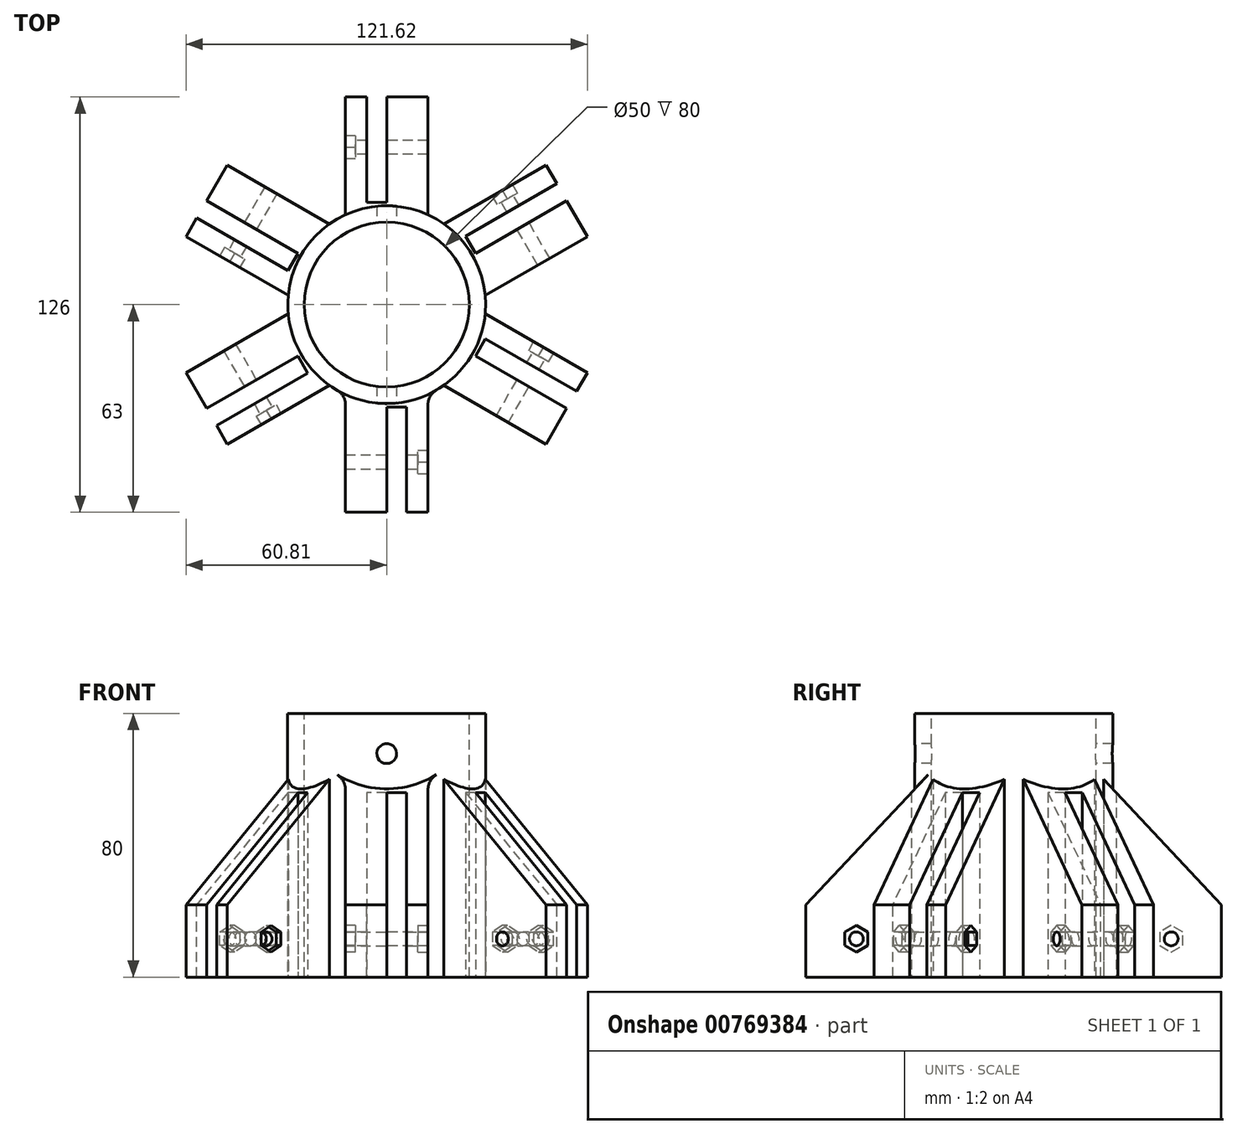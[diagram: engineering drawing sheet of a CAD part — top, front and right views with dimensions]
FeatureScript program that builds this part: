
annotation { "Feature Type Name" : "Feature", "Feature Type Description" : "" }
export const myFeature = defineFeature(function(context is Context, id is Id, definition is map)
    precondition{}
    {
        {
            var Q0;
            Q0=qCreatedBy(makeId("Top.planeOp"),FACE);
            var sketch = newSketch(context, id + "F0", { "sketchPlane" : qUnion([Q0])});
            skCircle(sketch, "E0", {"center": v(0, 0) * mm, "radius": 30 * mm});
            skSolve(sketch);
        }
        {
            var Q0;
            Q0=qSketchRegion(id+"F0",true);
            var Q1;
            Q1=qSketchRegion(id+"F2",true);
            extrude(context, id + "F1", {"entities" : qUnion([Q0, Q1]), "depth" : 60 * mm, "offsetDistance" : 25 * mm});
        }
        {
            var Q0;
            Q0=qCreatedBy(makeId("Front.planeOp"),FACE);
            var sketch = newSketch(context, id + "F2", { "sketchPlane" : qUnion([Q0])});
            skLineSegment(sketch, "E1.bottom", {"start": v(-12.5, 0) * mm, "end": v(12.5, 0) * mm});
            skLineSegment(sketch, "E1.top", {"start": v(-12.5, 60) * mm, "end": v(12.5, 60) * mm});
            skLineSegment(sketch, "E1.left", {"start": v(-12.5, 0) * mm, "end": v(-12.5, 60) * mm});
            skLineSegment(sketch, "E1.right", {"start": v(12.5, 0) * mm, "end": v(12.5, 60) * mm});
            skSolve(sketch);
        }
        {
            var Q0;
            Q0=qSketchRegion(id+"F2",true);
            var Q1;
            Q1=qSketchRegion(id+"F4",true);
            extrude(context, id + "F3", {"entities" : qUnion([Q0, Q1]), "operationType" : NewBodyOperationType.ADD, "depth" : 63 * mm, "offsetDistance" : 25 * mm});
        }
        {
            var Q0;
            Q0=makeQuery(id+"F3.opExtrude","SWEPT_FACE",FACE,{"disambiguationData":[OSD([sQuery(id+"F2.wireOp",EDGE,"E1.right")])]});
            var sketch = newSketch(context, id + "F4", { "sketchPlane" : qUnion([Q0])});
            skLineSegment(sketch, "E2", {"start": v(-27.27, 60) * mm, "end": v(-63, 21.96) * mm});
            skLineSegment(sketch, "E3", {"start": v(-63, 21.96) * mm, "end": v(-63, 60) * mm});
            skLineSegment(sketch, "E4", {"start": v(-63, 60) * mm, "end": v(-27.27, 60) * mm});
            skSolve(sketch);
        }
        {
            var Q0;
            Q0=qSketchRegion(id+"F4",true);
            var Q1;
            Q1=qSketchRegion(id+"FgFtPWKNHrMfXQx_1",true);
            extrude(context, id + "F5", {"entities" : qUnion([Q0, Q1]), "operationType" : NewBodyOperationType.REMOVE, "oppositeDirection" : true, "depth" : 25 * mm, "offsetDistance" : 25 * mm});
        }
        {
            var Q0;
            Q0=qCreatedBy(makeId("Top.planeOp"),FACE);
            var sketch = newSketch(context, id + "F6", { "sketchPlane" : qUnion([Q0])});
            skLineSegment(sketch, "E5.left", {"start": v(0, -31.08) * mm, "end": v(0, -63.76) * mm});
            skLineSegment(sketch, "E5.right", {"start": v(6, -31.08) * mm, "end": v(6, -63.76) * mm});
            skLineSegment(sketch, "E6.bottom", {"start": v(0, -31.08) * mm, "end": v(6, -31.08) * mm});
            skLineSegment(sketch, "E6.top", {"start": v(0, -63.76) * mm, "end": v(6, -63.76) * mm});
            skPoint(sketch, "E5.bottom.start.orphan", {"position": v(0, -30.09) * mm});
            skSolve(sketch);
        }
        {
            var Q0;
            Q0=qSketchRegion(id+"F6",true);
            var Q1;
            Q1=makeQuery(id+"F5.boolean.opBoolean","COPY",FACE,{"derivedFrom":makeQuery(id+"F5.opExtrude","SWEPT_FACE",FACE,{"disambiguationData":[OSD([sQuery(id+"F4.wireOp",EDGE,"E2")])]})});
            extrude(context, id + "F7", {"entities" : qUnion([Q0, Q1]), "operationType" : NewBodyOperationType.REMOVE, "depth" : 114.6 * mm, "offsetDistance" : 25 * mm});
        }
        {
            var Q0;
            Q0=makeQuery(id+"F3.opExtrude","SWEPT_FACE",FACE,{"disambiguationData":[OSD([sQuery(id+"F2.wireOp",EDGE,"E1.right")])]});
            var sketch = newSketch(context, id + "F8", { "sketchPlane" : qUnion([Q0])});
            skCircle(sketch, "E7", {"center": v(-47.71, 11.61) * mm, "radius": 2.1 * mm});
            skPoint(sketch, "E8.0.midPoint", {"position": v(-44.21, 11.61) * mm});
            skCircle(sketch, "E9.cCircle", {"center": v(-47.71, 11.61) * mm, "radius": 3.5 * mm, "construction": true});
            skLineSegment(sketch, "E9.0", {"start": v(-44.21, 13.63) * mm, "end": v(-44.21, 9.6) * mm});
            skLineSegment(sketch, "E9.1", {"start": v(-44.21, 9.6) * mm, "end": v(-47.71, 7.57) * mm});
            skLineSegment(sketch, "E9.2", {"start": v(-47.71, 7.57) * mm, "end": v(-51.21, 9.6) * mm});
            skLineSegment(sketch, "E9.3", {"start": v(-51.21, 9.6) * mm, "end": v(-51.21, 13.63) * mm});
            skLineSegment(sketch, "E9.4", {"start": v(-51.21, 13.63) * mm, "end": v(-47.71, 15.66) * mm});
            skLineSegment(sketch, "E9.5", {"start": v(-47.71, 15.66) * mm, "end": v(-44.21, 13.63) * mm});
            skSolve(sketch);
        }
        {
            var Q0;
            Q0 = qSketchRegion(id + "F8", true);
            extrude(context, id + "F9", {"entities" : qUnion([Q0]), "operationType" : NewBodyOperationType.REMOVE, "oppositeDirection" : true, "depth" : 3 * mm, "offsetDistance" : 25 * mm});
        }
        {
            var Q0;
            Q0=sQuery(id+"F8.wireOp",VERTEX,"XOagpPQl-PvC6-i4lp-4W3e-Tbm5HYOVrYsB.center");
            var Q1;
            Q1=sQuery(id+"F8.wireOp",VERTEX,"E7.center");
            var Q2;
            Q2=makeQuery(id+"F1.opExtrude","SWEPT_BODY",BODY,{"disambiguationData":[OSD([sQuery(id+"F0.wireOp",EDGE,"E0")])]});
            hole(context, id + "F10", {"style" : HoleStyle.SIMPLE, "endStyle" : HoleEndStyle.THROUGH, "holeDiameter" : 4.2 * mm, "majorDiameter" : 5 * mm, "isTappedThrough" : true, "tappedDepth" : 12 * mm, "tapClearance" : 3, "locations" : qUnion([Q0, Q1]), "scope" : qUnion([Q2])});
        }
        {
            var Q0;
            Q0=makeQuery(id+"F1.opExtrude","SWEPT_BODY",BODY,{"disambiguationData":[OSD([sQuery(id+"F0.wireOp",EDGE,"E0")])]});
            var Q1;
            Q1=makeQuery(id+"F1.opExtrude","SWEPT_FACE",FACE,{"disambiguationData":[OSD([sQuery(id+"F0.wireOp",EDGE,"E0")])]});
            circularPattern(context, id + "F11", {"operationType" : NewBodyOperationType.ADD, "entities" : qUnion([Q0]), "axis" : qUnion([Q1]), "angle" : 360 * degree, "instanceCount" : 6, "equalSpace" : true});
        }
        {
            var Q0;
            {var subQ0=makeQuery(id+"F3.boolean.opBoolean","MERGE",FACE,{"derivedFrom":[makeQuery(id+"F1.opExtrude","CAP_FACE",FACE,{"disambiguationData":[OSD([sQuery(id+"F0.wireOp",EDGE,"E0")])],"isStart":false}),makeQuery(id+"F3.opExtrude","SWEPT_FACE",FACE,{"disambiguationData":[OSD([sQuery(id+"F2.wireOp",EDGE,"E1.top")])]})]});Q0=makeQuery(id+"F11.boolean.opBoolean","MERGE",FACE,{"derivedFrom":[subQ0,makeQuery(id+"F11.opPattern","COPY",FACE,{"derivedFrom":subQ0,"instanceName":"1"}),makeQuery(id+"F11.opPattern","COPY",FACE,{"derivedFrom":subQ0,"instanceName":"2"}),makeQuery(id+"F11.opPattern","COPY",FACE,{"derivedFrom":subQ0,"instanceName":"3"}),makeQuery(id+"F11.opPattern","COPY",FACE,{"derivedFrom":subQ0,"instanceName":"4"}),makeQuery(id+"F11.opPattern","COPY",FACE,{"derivedFrom":subQ0,"instanceName":"5"})]});}
            var sketch = newSketch(context, id + "F12", { "sketchPlane" : qUnion([Q0])});
            skCircle(sketch, "E10", {"center": v(0, 0) * mm, "radius": 25 * mm});
            skSolve(sketch);
        }
        {
            var Q0;
            Q0=makeQuery(id+"F12.imprint","IMPRINT",FACE,{"disambiguationData":[TD([[makeQuery(id+"F12.imprint","IMPRINT",EDGE,{"derivedFrom":sQuery(id+"F12.wireOp",EDGE,"E10")}),1.0]])]});
            extrude(context, id + "F13", {"entities" : qUnion([Q0]), "operationType" : NewBodyOperationType.REMOVE, "endBound" : BoundingType.THROUGH_ALL, "oppositeDirection" : true, "depth" : 25 * mm, "offsetDistance" : 25 * mm});
        }
        {
            var Q0;
            {var subQ0=makeQuery(id+"F3.boolean.opBoolean","MERGE",FACE,{"derivedFrom":[makeQuery(id+"F1.opExtrude","CAP_FACE",FACE,{"disambiguationData":[OSD([sQuery(id+"F0.wireOp",EDGE,"E0")])],"isStart":false}),makeQuery(id+"F3.opExtrude","SWEPT_FACE",FACE,{"disambiguationData":[OSD([sQuery(id+"F2.wireOp",EDGE,"E1.top")])]})]});Q0=makeQuery(id+"F11.boolean.opBoolean","MERGE",FACE,{"derivedFrom":[subQ0,makeQuery(id+"F11.opPattern","COPY",FACE,{"derivedFrom":subQ0,"instanceName":"1"}),makeQuery(id+"F11.opPattern","COPY",FACE,{"derivedFrom":subQ0,"instanceName":"2"}),makeQuery(id+"F11.opPattern","COPY",FACE,{"derivedFrom":subQ0,"instanceName":"3"}),makeQuery(id+"F11.opPattern","COPY",FACE,{"derivedFrom":subQ0,"instanceName":"4"}),makeQuery(id+"F11.opPattern","COPY",FACE,{"derivedFrom":subQ0,"instanceName":"5"})]});}
            extrude(context, id + "F14", {"entities" : qUnion([Q0]), "operationType" : NewBodyOperationType.ADD, "depth" : 20 * mm, "offsetDistance" : 25 * mm});
        }
        {
            var Q0;
            Q0=makeQuery(id+"F3.boolean.opBoolean","INTERSECT",EDGE,{"derivedFrom":[makeQuery(id+"F1.opExtrude","SWEPT_FACE",FACE,{"disambiguationData":[OSD([sQuery(id+"F0.wireOp",EDGE,"E0")])]}),makeQuery(id+"F3.opExtrude","SWEPT_FACE",FACE,{"disambiguationData":[OSD([sQuery(id+"F2.wireOp",EDGE,"E1.right")])]})]});
            var Q1;
            {var subQ0=makeQuery(id+"F1.opExtrude","SWEPT_FACE",FACE,{"disambiguationData":[OSD([sQuery(id+"F0.wireOp",EDGE,"E0")])]});var subQ1=subQ0;Q1=makeQuery(id+"F11.boolean.opBoolean","INTERSECT",EDGE,{"disambiguationData":[topologyDisambiguationEdgeConnected([makeQuery(id+"F11.opPattern","COPY",FACE,{"derivedFrom":makeQuery(id+"F3.opExtrude","SWEPT_FACE",FACE,{"disambiguationData":[OSD([sQuery(id+"F2.wireOp",EDGE,"E1.left")])]}),"instanceName":"5"})])],"derivedFrom":[makeQuery(id+"F11.opPattern","COPY",FACE,{"derivedFrom":subQ1,"instanceName":"1"}),makeQuery(id+"F11.opPattern","COPY",FACE,{"derivedFrom":subQ1,"instanceName":"2"}),makeQuery(id+"F11.opPattern","COPY",FACE,{"derivedFrom":subQ1,"instanceName":"3"}),makeQuery(id+"F11.opPattern","COPY",FACE,{"derivedFrom":subQ1,"instanceName":"4"})]});}
            var Q2;
            Q2=makeQuery(id+"F3.boolean.opBoolean","INTERSECT",EDGE,{"derivedFrom":[makeQuery(id+"F1.opExtrude","SWEPT_FACE",FACE,{"disambiguationData":[OSD([sQuery(id+"F0.wireOp",EDGE,"E0")])]}),makeQuery(id+"F3.opExtrude","SWEPT_FACE",FACE,{"disambiguationData":[OSD([sQuery(id+"F2.wireOp",EDGE,"E1.left")])]})]});
            var Q3;
            Q3=makeQuery(id+"F11.opPattern","COPY",EDGE,{"derivedFrom":makeQuery(id+"F3.boolean.opBoolean","INTERSECT",EDGE,{"derivedFrom":[makeQuery(id+"F1.opExtrude","SWEPT_FACE",FACE,{"disambiguationData":[OSD([sQuery(id+"F0.wireOp",EDGE,"E0")])]}),makeQuery(id+"F3.opExtrude","SWEPT_FACE",FACE,{"disambiguationData":[OSD([sQuery(id+"F2.wireOp",EDGE,"E1.right")])]})]}),"instanceName":"1"});
            var Q4;
            {var subQ0=sQuery(id+"F0.wireOp",EDGE,"E0");var subQ1=makeQuery(id+"F1.opExtrude","SWEPT_FACE",FACE,{"disambiguationData":[OSD([subQ0])]});var subQ3=sQuery(id+"F2.wireOp",EDGE,"E1.right");var subQ5=subQ1;Q4=makeQuery(id+"F11.boolean.opBoolean","INTERSECT",EDGE,{"disambiguationData":[topologyDisambiguationEdgeConnected([makeQuery(id+"F11.opPattern","COPY",FACE,{"derivedFrom":makeQuery(id+"F9.boolean.opBoolean","SPLIT",FACE,{"disambiguationData":[TD([subQ1])],"derivedFrom":makeQuery(id+"F3.opExtrude","SWEPT_FACE",FACE,{"disambiguationData":[OSD([subQ3])]})}),"instanceName":"2"})])],"derivedFrom":[makeQuery(id+"F11.opPattern","COPY",FACE,{"derivedFrom":subQ5,"instanceName":"1"}),makeQuery(id+"F11.opPattern","COPY",FACE,{"derivedFrom":subQ5,"instanceName":"3"})]});}
            var Q5;
            Q5=makeQuery(id+"F11.opPattern","COPY",EDGE,{"derivedFrom":makeQuery(id+"F3.boolean.opBoolean","INTERSECT",EDGE,{"derivedFrom":[makeQuery(id+"F1.opExtrude","SWEPT_FACE",FACE,{"disambiguationData":[OSD([sQuery(id+"F0.wireOp",EDGE,"E0")])]}),makeQuery(id+"F3.opExtrude","SWEPT_FACE",FACE,{"disambiguationData":[OSD([sQuery(id+"F2.wireOp",EDGE,"E1.left")])]})]}),"instanceName":"1"});
            var Q6;
            {var subQ0=makeQuery(id+"F1.opExtrude","SWEPT_FACE",FACE,{"disambiguationData":[OSD([sQuery(id+"F0.wireOp",EDGE,"E0")])]});var subQ1=subQ0;Q6=makeQuery(id+"F11.boolean.opBoolean","INTERSECT",EDGE,{"disambiguationData":[topologyDisambiguationEdgeConnected([makeQuery(id+"F11.opPattern","COPY",FACE,{"derivedFrom":makeQuery(id+"F3.opExtrude","SWEPT_FACE",FACE,{"disambiguationData":[OSD([sQuery(id+"F2.wireOp",EDGE,"E1.left")])]}),"instanceName":"2"})])],"derivedFrom":[makeQuery(id+"F11.opPattern","COPY",FACE,{"derivedFrom":subQ1,"instanceName":"1"}),makeQuery(id+"F11.opPattern","COPY",FACE,{"derivedFrom":subQ1,"instanceName":"3"})]});}
            var Q7;
            {var subQ0=sQuery(id+"F0.wireOp",EDGE,"E0");var subQ1=makeQuery(id+"F1.opExtrude","SWEPT_FACE",FACE,{"disambiguationData":[OSD([subQ0])]});var subQ3=sQuery(id+"F2.wireOp",EDGE,"E1.right");var subQ5=subQ1;Q7=makeQuery(id+"F11.boolean.opBoolean","INTERSECT",EDGE,{"disambiguationData":[topologyDisambiguationEdgeConnected([makeQuery(id+"F11.opPattern","COPY",FACE,{"derivedFrom":makeQuery(id+"F9.boolean.opBoolean","SPLIT",FACE,{"disambiguationData":[TD([subQ1])],"derivedFrom":makeQuery(id+"F3.opExtrude","SWEPT_FACE",FACE,{"disambiguationData":[OSD([subQ3])]})}),"instanceName":"3"})])],"derivedFrom":[makeQuery(id+"F11.opPattern","COPY",FACE,{"derivedFrom":subQ5,"instanceName":"1"}),makeQuery(id+"F11.opPattern","COPY",FACE,{"derivedFrom":subQ5,"instanceName":"2"}),makeQuery(id+"F11.opPattern","COPY",FACE,{"derivedFrom":subQ5,"instanceName":"4"})]});}
            var Q8;
            {var subQ0=makeQuery(id+"F1.opExtrude","SWEPT_FACE",FACE,{"disambiguationData":[OSD([sQuery(id+"F0.wireOp",EDGE,"E0")])]});var subQ1=subQ0;Q8=makeQuery(id+"F11.boolean.opBoolean","INTERSECT",EDGE,{"disambiguationData":[topologyDisambiguationEdgeConnected([makeQuery(id+"F11.opPattern","COPY",FACE,{"derivedFrom":makeQuery(id+"F3.opExtrude","SWEPT_FACE",FACE,{"disambiguationData":[OSD([sQuery(id+"F2.wireOp",EDGE,"E1.left")])]}),"instanceName":"3"})])],"derivedFrom":[makeQuery(id+"F11.opPattern","COPY",FACE,{"derivedFrom":subQ1,"instanceName":"1"}),makeQuery(id+"F11.opPattern","COPY",FACE,{"derivedFrom":subQ1,"instanceName":"2"}),makeQuery(id+"F11.opPattern","COPY",FACE,{"derivedFrom":subQ1,"instanceName":"4"})]});}
            var Q9;
            {var subQ0=sQuery(id+"F0.wireOp",EDGE,"E0");var subQ1=makeQuery(id+"F1.opExtrude","SWEPT_FACE",FACE,{"disambiguationData":[OSD([subQ0])]});var subQ3=sQuery(id+"F2.wireOp",EDGE,"E1.right");var subQ5=subQ1;Q9=makeQuery(id+"F11.boolean.opBoolean","INTERSECT",EDGE,{"disambiguationData":[topologyDisambiguationEdgeConnected([makeQuery(id+"F11.opPattern","COPY",FACE,{"derivedFrom":makeQuery(id+"F9.boolean.opBoolean","SPLIT",FACE,{"disambiguationData":[TD([subQ1])],"derivedFrom":makeQuery(id+"F3.opExtrude","SWEPT_FACE",FACE,{"disambiguationData":[OSD([subQ3])]})}),"instanceName":"4"})])],"derivedFrom":[makeQuery(id+"F11.opPattern","COPY",FACE,{"derivedFrom":subQ5,"instanceName":"1"}),makeQuery(id+"F11.opPattern","COPY",FACE,{"derivedFrom":subQ5,"instanceName":"2"}),makeQuery(id+"F11.opPattern","COPY",FACE,{"derivedFrom":subQ5,"instanceName":"3"}),makeQuery(id+"F11.opPattern","COPY",FACE,{"derivedFrom":subQ5,"instanceName":"5"})]});}
            var Q10;
            {var subQ0=sQuery(id+"F0.wireOp",EDGE,"E0");var subQ1=makeQuery(id+"F1.opExtrude","SWEPT_FACE",FACE,{"disambiguationData":[OSD([subQ0])]});var subQ3=sQuery(id+"F2.wireOp",EDGE,"E1.right");var subQ5=subQ1;Q10=makeQuery(id+"F11.boolean.opBoolean","INTERSECT",EDGE,{"disambiguationData":[topologyDisambiguationEdgeConnected([makeQuery(id+"F11.opPattern","COPY",FACE,{"derivedFrom":makeQuery(id+"F9.boolean.opBoolean","SPLIT",FACE,{"disambiguationData":[TD([subQ1])],"derivedFrom":makeQuery(id+"F3.opExtrude","SWEPT_FACE",FACE,{"disambiguationData":[OSD([subQ3])]})}),"instanceName":"5"})])],"derivedFrom":[makeQuery(id+"F11.opPattern","COPY",FACE,{"derivedFrom":subQ5,"instanceName":"1"}),makeQuery(id+"F11.opPattern","COPY",FACE,{"derivedFrom":subQ5,"instanceName":"2"}),makeQuery(id+"F11.opPattern","COPY",FACE,{"derivedFrom":subQ5,"instanceName":"3"}),makeQuery(id+"F11.opPattern","COPY",FACE,{"derivedFrom":subQ5,"instanceName":"4"})]});}
            var Q11;
            {var subQ0=makeQuery(id+"F1.opExtrude","SWEPT_FACE",FACE,{"disambiguationData":[OSD([sQuery(id+"F0.wireOp",EDGE,"E0")])]});var subQ1=subQ0;Q11=makeQuery(id+"F11.boolean.opBoolean","INTERSECT",EDGE,{"disambiguationData":[topologyDisambiguationEdgeConnected([makeQuery(id+"F11.opPattern","COPY",FACE,{"derivedFrom":makeQuery(id+"F3.opExtrude","SWEPT_FACE",FACE,{"disambiguationData":[OSD([sQuery(id+"F2.wireOp",EDGE,"E1.left")])]}),"instanceName":"4"})])],"derivedFrom":[makeQuery(id+"F11.opPattern","COPY",FACE,{"derivedFrom":subQ1,"instanceName":"1"}),makeQuery(id+"F11.opPattern","COPY",FACE,{"derivedFrom":subQ1,"instanceName":"2"}),makeQuery(id+"F11.opPattern","COPY",FACE,{"derivedFrom":subQ1,"instanceName":"3"}),makeQuery(id+"F11.opPattern","COPY",FACE,{"derivedFrom":subQ1,"instanceName":"5"})]});}
            fillet(context, id + "F15", {"entities" : qUnion([Q0, Q1, Q2, Q3, Q4, Q5, Q6, Q7, Q8, Q9, Q10, Q11]), "radius" : 5 * mm, "tangentPropagation" : true, "allowEdgeOverflow" : false});
        }
        {
            var Q0;
            Q0=qCreatedBy(makeId("Front.planeOp"),FACE);
            var sketch = newSketch(context, id + "F16", { "sketchPlane" : qUnion([Q0])});
            skCircle(sketch, "E11", {"center": v(0, 67.8) * mm, "radius": 3 * mm});
            skCircle(sketch, "E12.cCircle", {"center": v(0, 67.8) * mm, "radius": 5 * mm, "construction": true});
            skLineSegment(sketch, "E12.0", {"start": v(5, 70.68) * mm, "end": v(5, 64.9) * mm});
            skLineSegment(sketch, "E12.1", {"start": v(5, 64.9) * mm, "end": v(0, 62.02) * mm});
            skLineSegment(sketch, "E12.2", {"start": v(0, 62.02) * mm, "end": v(-5, 64.9) * mm});
            skLineSegment(sketch, "E12.3", {"start": v(-5, 64.9) * mm, "end": v(-5, 70.68) * mm});
            skLineSegment(sketch, "E12.4", {"start": v(-5, 70.68) * mm, "end": v(0, 73.57) * mm});
            skLineSegment(sketch, "E12.5", {"start": v(0, 73.57) * mm, "end": v(5, 70.68) * mm});
            skPoint(sketch, "E12.0.midPoint", {"position": v(5, 67.8) * mm});
            skSolve(sketch);
        }
        {
            var Q0;
            Q0=makeQuery(id+"F16.imprint","IMPRINT",FACE,{"disambiguationData":[TD([[makeQuery(id+"F16.imprint","IMPRINT",EDGE,{"derivedFrom":sQuery(id+"F16.wireOp",EDGE,"E11")}),1.0]])]});
            extrude(context, id + "F17", {"entities" : qUnion([Q0]), "operationType" : NewBodyOperationType.REMOVE, "endBound" : BoundingType.SYMMETRIC, "oppositeDirection" : true, "depth" : 76.6 * mm, "offsetDistance" : 25 * mm});
        }
    });
